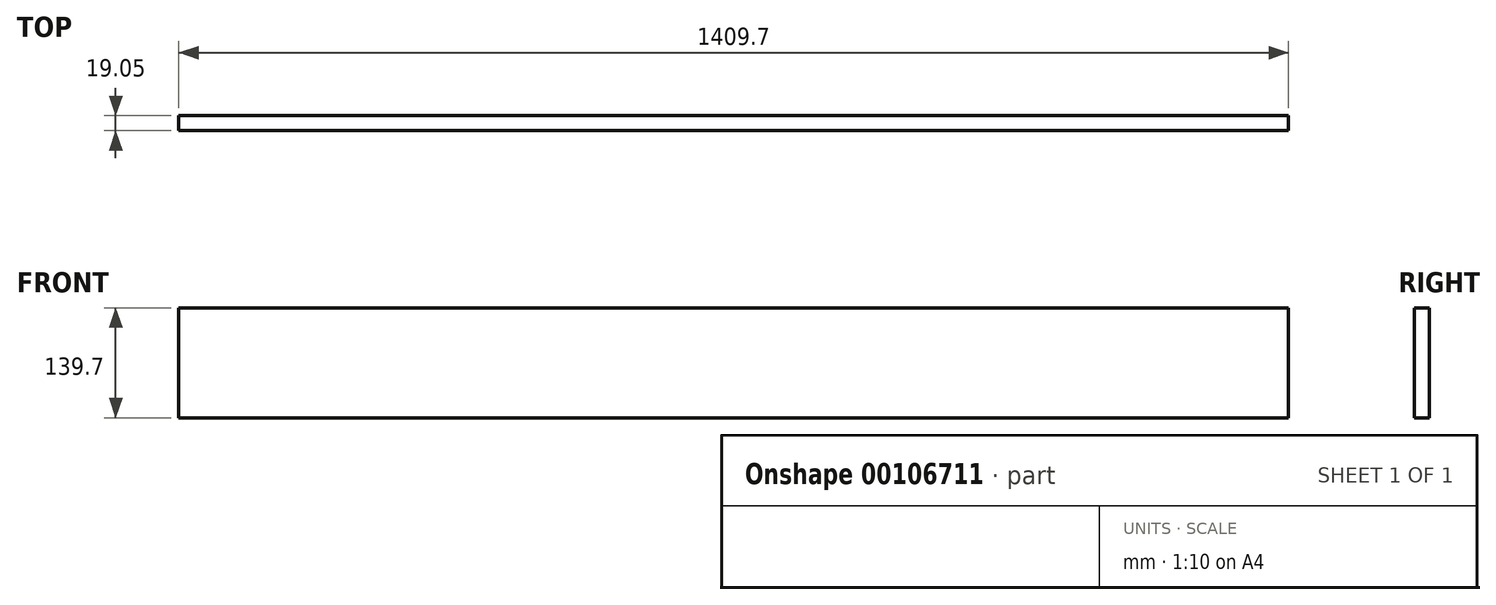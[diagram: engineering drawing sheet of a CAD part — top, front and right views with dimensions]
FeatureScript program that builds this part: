
annotation { "Feature Type Name" : "Feature", "Feature Type Description" : "" }
export const myFeature = defineFeature(function(context is Context, id is Id, definition is map)
    precondition{}
    {
        {
            var Q0;
            Q0=qCreatedBy(makeId("Front.planeOp"),FACE);
            var sketch = newSketch(context, id + "F0", { "sketchPlane" : qUnion([Q0])});
            skLineSegment(sketch, "E0.bottom", {"start": v(0, 0) * mm, "end": v(1409.7, 0) * mm});
            skLineSegment(sketch, "E0.top", {"start": v(0, 139.7) * mm, "end": v(1409.7, 139.7) * mm});
            skLineSegment(sketch, "E0.left", {"start": v(0, 0) * mm, "end": v(0, 139.7) * mm});
            skLineSegment(sketch, "E0.right", {"start": v(1409.7, 0) * mm, "end": v(1409.7, 139.7) * mm});
            skSolve(sketch);
        }
        {
            var Q0;
            Q0=makeQuery(id+"F0.imprint","IMPRINT",FACE,{"disambiguationData":[TD([[makeQuery(id+"F0.imprint","IMPRINT",EDGE,{"derivedFrom":sQuery(id+"F0.wireOp",EDGE,"E0.bottom")}),1.0]])]});
            extrude(context, id + "F1", {"entities" : qUnion([Q0]), "depth" : 19.05 * mm});
        }
    });
